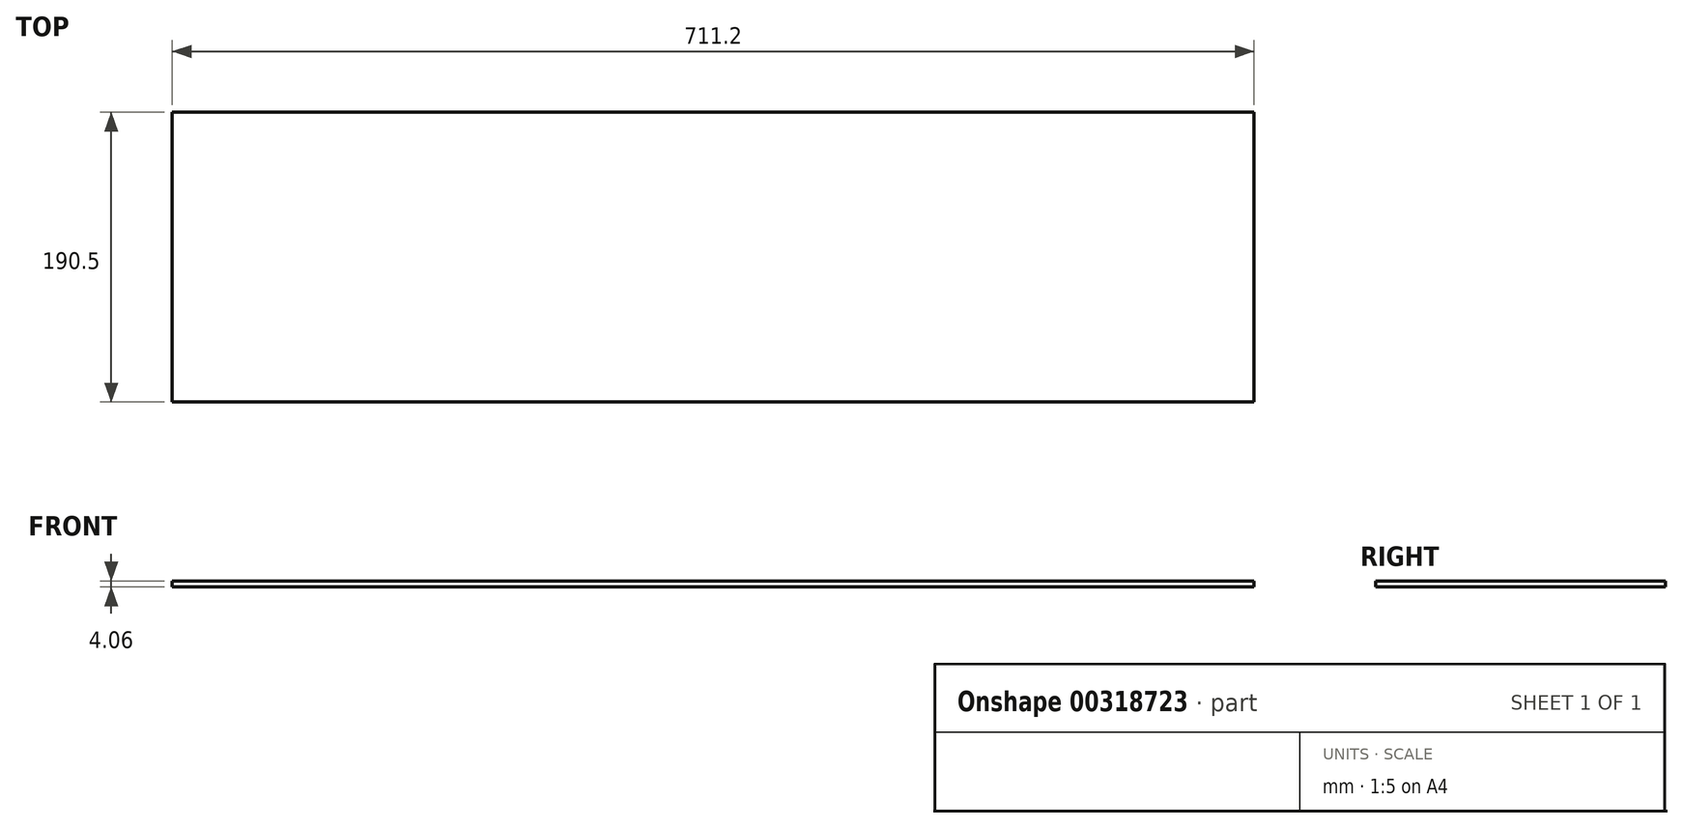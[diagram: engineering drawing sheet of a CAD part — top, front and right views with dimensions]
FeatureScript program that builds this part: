
annotation { "Feature Type Name" : "Feature", "Feature Type Description" : "" }
export const myFeature = defineFeature(function(context is Context, id is Id, definition is map)
    precondition{}
    {
        {
            var Q0;
            Q0=qCreatedBy(makeId("Top.planeOp"),FACE);
            var sketch = newSketch(context, id + "F0", { "sketchPlane" : qUnion([Q0])});
            skLineSegment(sketch, "E0.bottom", {"start": v(0, 0) * mm, "end": v(711.2, 0) * mm});
            skLineSegment(sketch, "E0.top", {"start": v(0, 190.5) * mm, "end": v(711.2, 190.5) * mm});
            skLineSegment(sketch, "E0.left", {"start": v(0, 0) * mm, "end": v(0, 190.5) * mm});
            skLineSegment(sketch, "E0.right", {"start": v(711.2, 0) * mm, "end": v(711.2, 190.5) * mm});
            skSolve(sketch);
        }
        {
            var Q0;
            Q0 = qSketchRegion(id + "F0", true);
            extrude(context, id + "F1", {"entities" : qUnion([Q0]), "depth" : 4.06 * mm});
        }
    });
